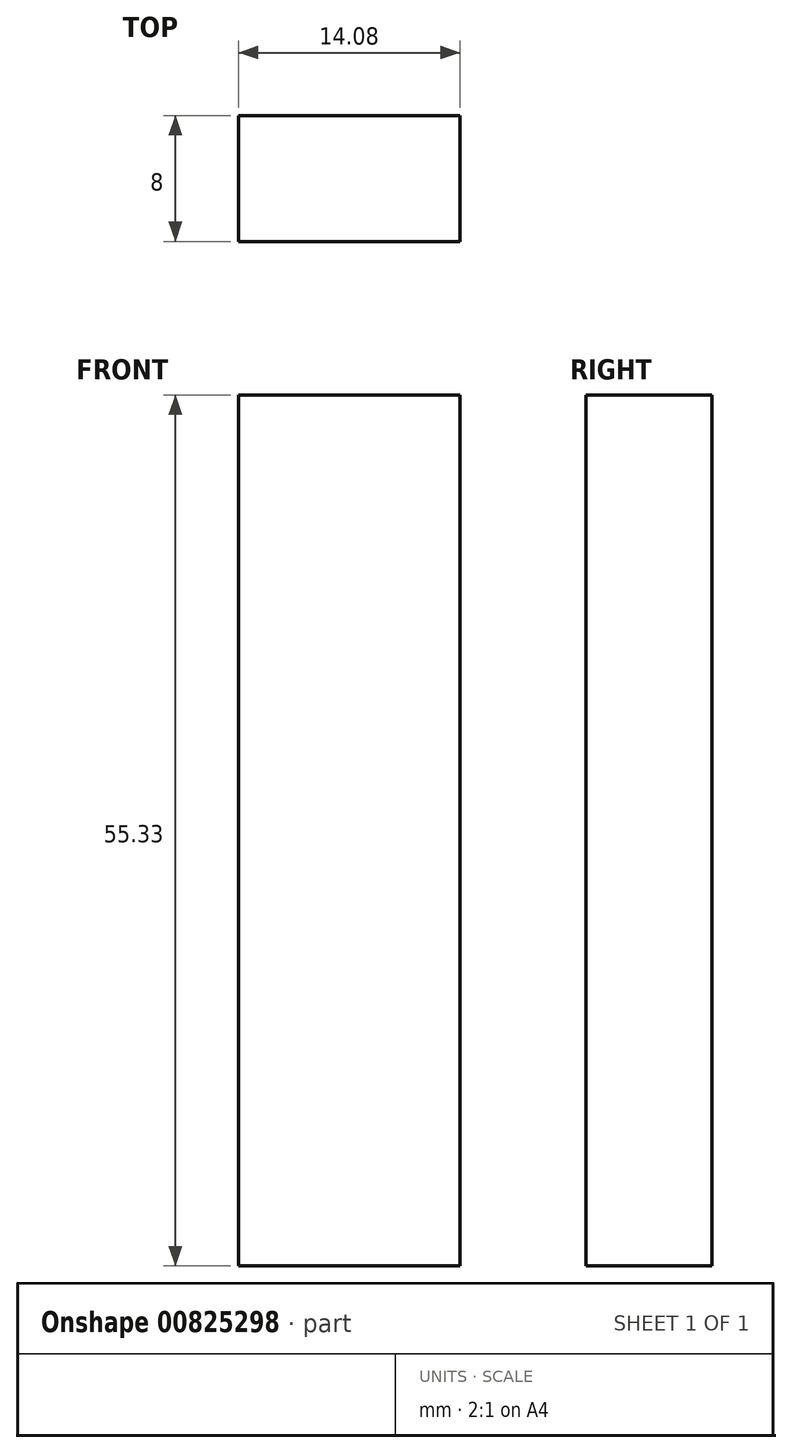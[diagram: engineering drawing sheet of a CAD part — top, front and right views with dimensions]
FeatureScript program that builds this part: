
annotation { "Feature Type Name" : "Feature", "Feature Type Description" : "" }
export const myFeature = defineFeature(function(context is Context, id is Id, definition is map)
    precondition{}
    {
        {
            var Q0;
            Q0=qCreatedBy(makeId("Front.planeOp"),FACE);
            var sketch = newSketch(context, id + "F0", { "sketchPlane" : qUnion([Q0])});
            skLineSegment(sketch, "E0.bottom", {"start": v(-57.05, 55.33) * mm, "end": v(-42.97, 55.33) * mm});
            skLineSegment(sketch, "E0.top", {"start": v(-57.05, 0) * mm, "end": v(-42.97, 0) * mm});
            skLineSegment(sketch, "E0.left", {"start": v(-57.05, 55.33) * mm, "end": v(-57.05, 0) * mm});
            skLineSegment(sketch, "E0.right", {"start": v(-42.97, 55.33) * mm, "end": v(-42.97, 0) * mm});
            skSolve(sketch);
        }
        {
            var Q0;
            Q0=makeQuery(id+"F0.imprint","IMPRINT",FACE,{"disambiguationData":[TD([[makeQuery(id+"F0.imprint","IMPRINT",EDGE,{"derivedFrom":sQuery(id+"F0.wireOp",EDGE,"E0.bottom")}),-1.0]])]});
            extrude(context, id + "F1", {"entities" : qUnion([Q0]), "depth" : 8 * mm, "offsetDistance" : 25 * mm});
        }
    });
